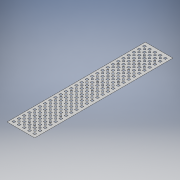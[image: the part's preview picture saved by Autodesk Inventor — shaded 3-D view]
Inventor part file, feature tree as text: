
AUTODESK INVENTOR PART (.ipt)
format: ipt  version: 2018 (Build 220112000, 112)  size: 1,003,008 bytes
history: native  units: in
note: dims shown in document units (in); Inventor stores cm internally (conversion verified against a paired STEP export)
features: extrude x2, sketch x2
ambient origin geometry x8: Origin, YZ Plane, XZ Plane, XY Plane, X Axis, Y Axis, Z Axis, Center Point
bodies: Solid1 (feature_tree)
feature tree (4):
  extrude  "Extrusion1"  Depth=12.4016in
  extrude  "Extrusion2"  Depth=0.18in
  sketch  "Sketch1"  dims[d0=2.4803in d1=12.4016in]
  sketch  "Sketch2"  dims[d2=0.0039in d3=0.0in d4=0.18in d5=0.18in d6=10.2362in d8=0.4685in d9=1.9685in d11=0.4685in d14=0.0039in d15=0.0in]
